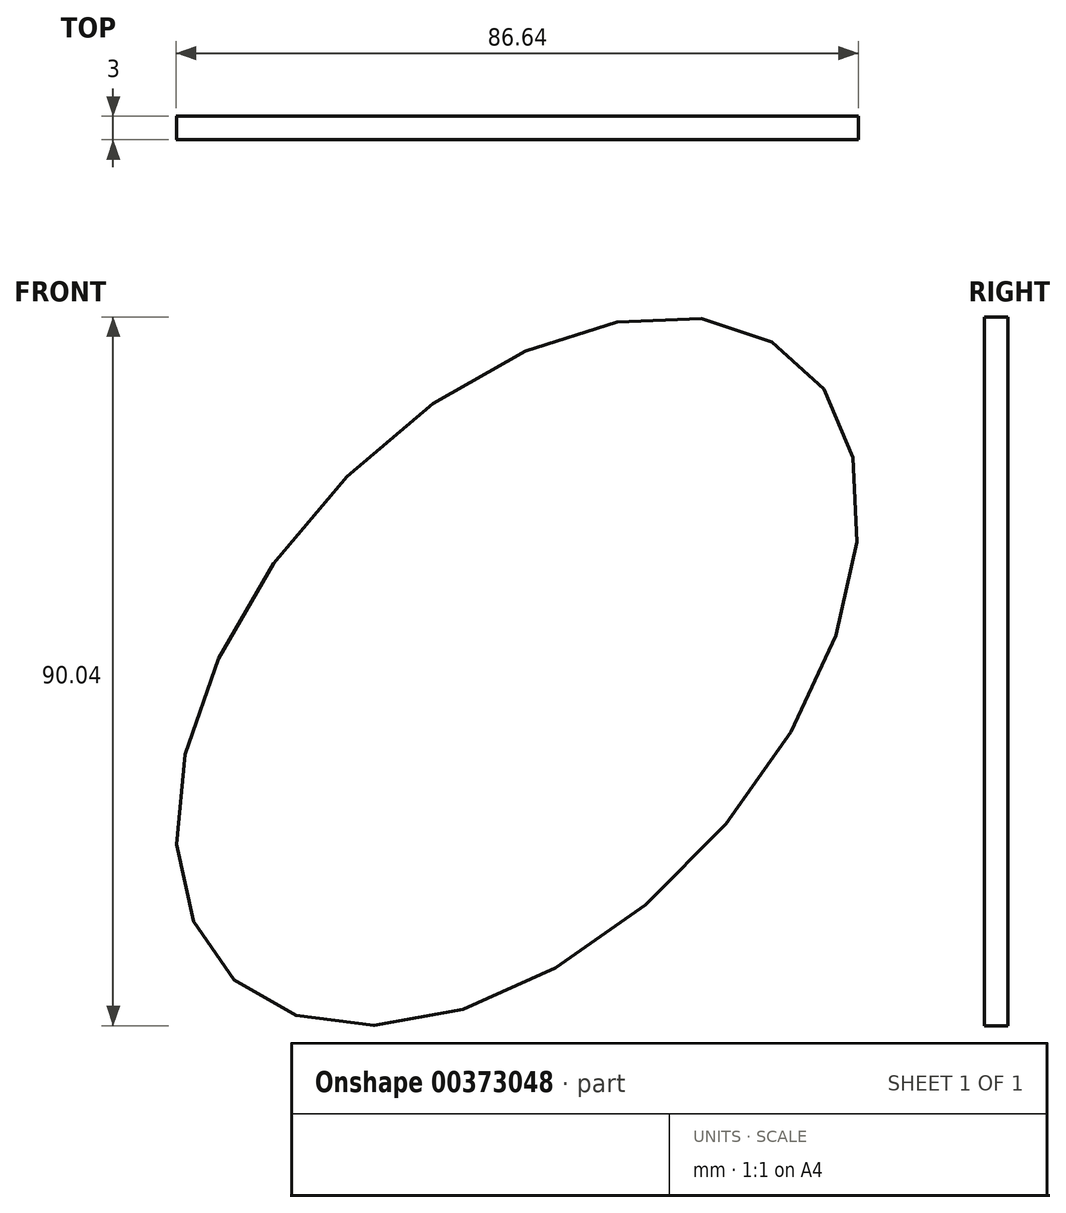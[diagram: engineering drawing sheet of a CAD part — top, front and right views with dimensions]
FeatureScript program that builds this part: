
annotation { "Feature Type Name" : "Feature", "Feature Type Description" : "" }
export const myFeature = defineFeature(function(context is Context, id is Id, definition is map)
    precondition{}
    {
        {
            var Q0;
            Q0=qCreatedBy(makeId("Front.planeOp"),FACE);
            var sketch = newSketch(context, id + "F0", { "sketchPlane" : qUnion([Q0])});
            skEllipse(sketch, "E0", {"center": v(0, 0) * mm, "majorRadius": 32.74 * mm, "minorRadius": 53.21 * mm, "majorAxis": v(-0.74, 0.68)});
            skSolve(sketch);
        }
        {
            var Q0;
            Q0=makeQuery(id+"F0.imprint","IMPRINT",FACE,{"disambiguationData":[TD([[makeQuery(id+"F0.imprint","IMPRINT",EDGE,{"derivedFrom":sQuery(id+"F0.wireOp",EDGE,"E0")}),1.0]])]});
            extrude(context, id + "F1", {"entities" : qUnion([Q0]), "depth" : 3 * mm});
        }
    });
